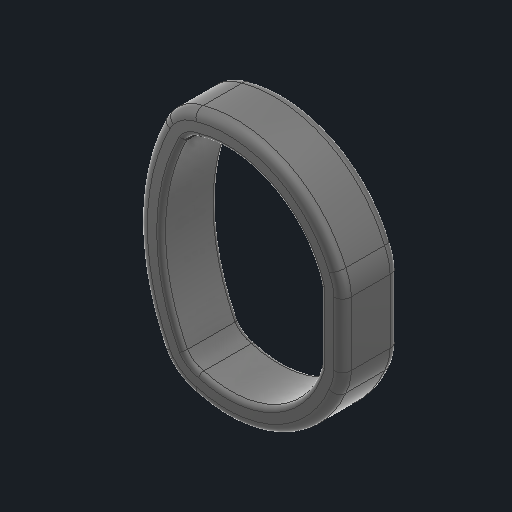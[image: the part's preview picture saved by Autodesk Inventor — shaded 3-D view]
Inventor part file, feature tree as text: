
AUTODESK INVENTOR PART (.ipt)
format: ipt  version: 2024 (Build 280153000, 153)  size: 416,256 bytes
history: native  units: in
note: dims shown in document units (in); Inventor stores cm internally (conversion verified against a paired STEP export)
features: other x3, sketch x1
ambient origin geometry x8: Origin, YZ Plane, XZ Plane, XY Plane, X Axis, Y Axis, Z Axis, Center Point
bodies: Solid1 (feature_tree)
feature tree (4):
  other  "ziptie.ipt"
  other  "Solid1::ziptie.ipt"
  other  "TaggingFeature1"
  sketch  "Sketch1"  dims[d0=0.3937in]
